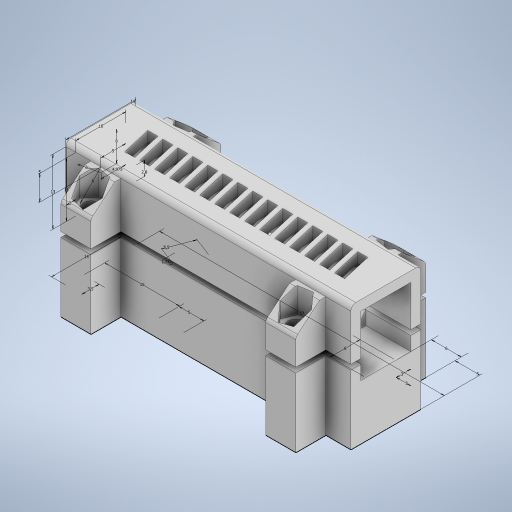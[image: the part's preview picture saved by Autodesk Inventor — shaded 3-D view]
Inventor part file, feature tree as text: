
AUTODESK INVENTOR PART (.ipt)
format: ipt  version: 2023 (Build 270158000, 158)  size: 687,104 bytes
history: native  units: in
note: dims shown in document units (in); Inventor stores cm internally (conversion verified against a paired STEP export)
features: extrude x8, sketch x4, chamfer x4, fillet x2, other x1, hole x1, split x1, move_body x1
ambient origin geometry x8: Origin, YZ Plane, XZ Plane, XY Plane, X Axis, Y Axis, Z Axis, Center Point
bodies: Solid6 (feature_tree), Solid7 (feature_tree)
feature tree (22):
  other  "Bryła1"
  sketch  "Szkic1"
  extrude  "Wyciągnięcie proste1"  Depth=0.5512in
  sketch  "Szkic2"
  extrude  "Wyciągnięcie proste2"  Depth=0.2362in
  extrude  "Wyciągnięcie proste4"  Depth=0.1969in
  hole  "Otwór1"  [1 undecoded]
  extrude  "Wyciągnięcie proste5"  Depth=0.0787in
  chamfer  "Faza1"  Distance=0.4331in
  chamfer  "Faza2"  Distance=0.3937in
  chamfer  "Faza3"  Distance=0.4331in
  chamfer  "Faza4"  Distance=0.5118in
  fillet  "Zaokrąglenie1"  Radius=2.2441in
  fillet  "Zaokrąglenie2"  Radius=0.0787in
  sketch  "Sketch7"  dims[d0=2.2441in d1=0.5512in]
  extrude  "Extrusion16"  Depth=0.5512in
  extrude  "Extrusion17"  Depth=0.0787in
  extrude  "Extrusion18"  Depth=0.1969in
  split  "Split3"
  move_body  "Move Body3"
  extrude  "Extrusion19"  Depth=0.0787in
  sketch  "Sketch8"  dims[d2=0.2362in d3=0.2362in d4=0.1969in d5=0.1181in d6=0.1181in d7=0.4331in d8=0.0in d9=0.3937in d10=0.4331in d11=0.5118in d12=2.2441in d13=0.0in d14=0.0787in d15=0.5512in d16=0.5906in d17=0.1969in d18=0.1378in d19=0.2165in d20=0.0682in d23=0.9055in d24=0.0in d25=0.126in d26=0.2362in d27=0.4331in d28=0.1024in d29=90.0deg d30=0.315in d31=0.8108in d32=0.1969in d33=0.0in d34=0.1575in d35=0.0787in d36=0.3436in d37=0.1575in d38=0.0787in d39=0.3436in d40=0.1575in d41=0.0787in d42=0.3436in d43=0.1575in d44=0.0787in d45=0.3436in d46=0.0394in d65=0.0394in d69=0.4724in d70=0.2362in d72=0.2362in d95=0.0787in d96=0.1181in d97=0.0787in d98=0.1181in d99=0.2057in d100=0.5291in d101=5.9055in d103=0.1181in d104=0.3937in d106=0.3937in d110=0.1102in d112=0.1969in d113=0.1969in d114=0.4724in d115=0.2362in d116=0.1959in d125=0.3543in d126=0.0in d127=0.3543in d128=0.0in d129=0.1181in d130=0.0in d131=0.0in d132=0.0394in d133=0.0in d134=0.0787in d135=0.0787in d136=90.0deg d137=0.6102in d138=0.0787in d139=0.0in d62=0.0197in d63=0.0344in d64=0.0197in d74=0.0197in d75=0.0344in d76=0.0197in d77=0.0344in d90=0.0197in d91=0.0344in d92=0.0197in d93=0.0344in d111=0.0344in d121=0.0197in d122=0.0344in d123=0.0197in d124=0.0344in d140=0.0197in d141=0.0344in]
note: 1 required parameter value undecoded (feature->parameter linkage not recoverable at this tier; creation-order binding heuristic only, values carry confidence <= 0.55)
